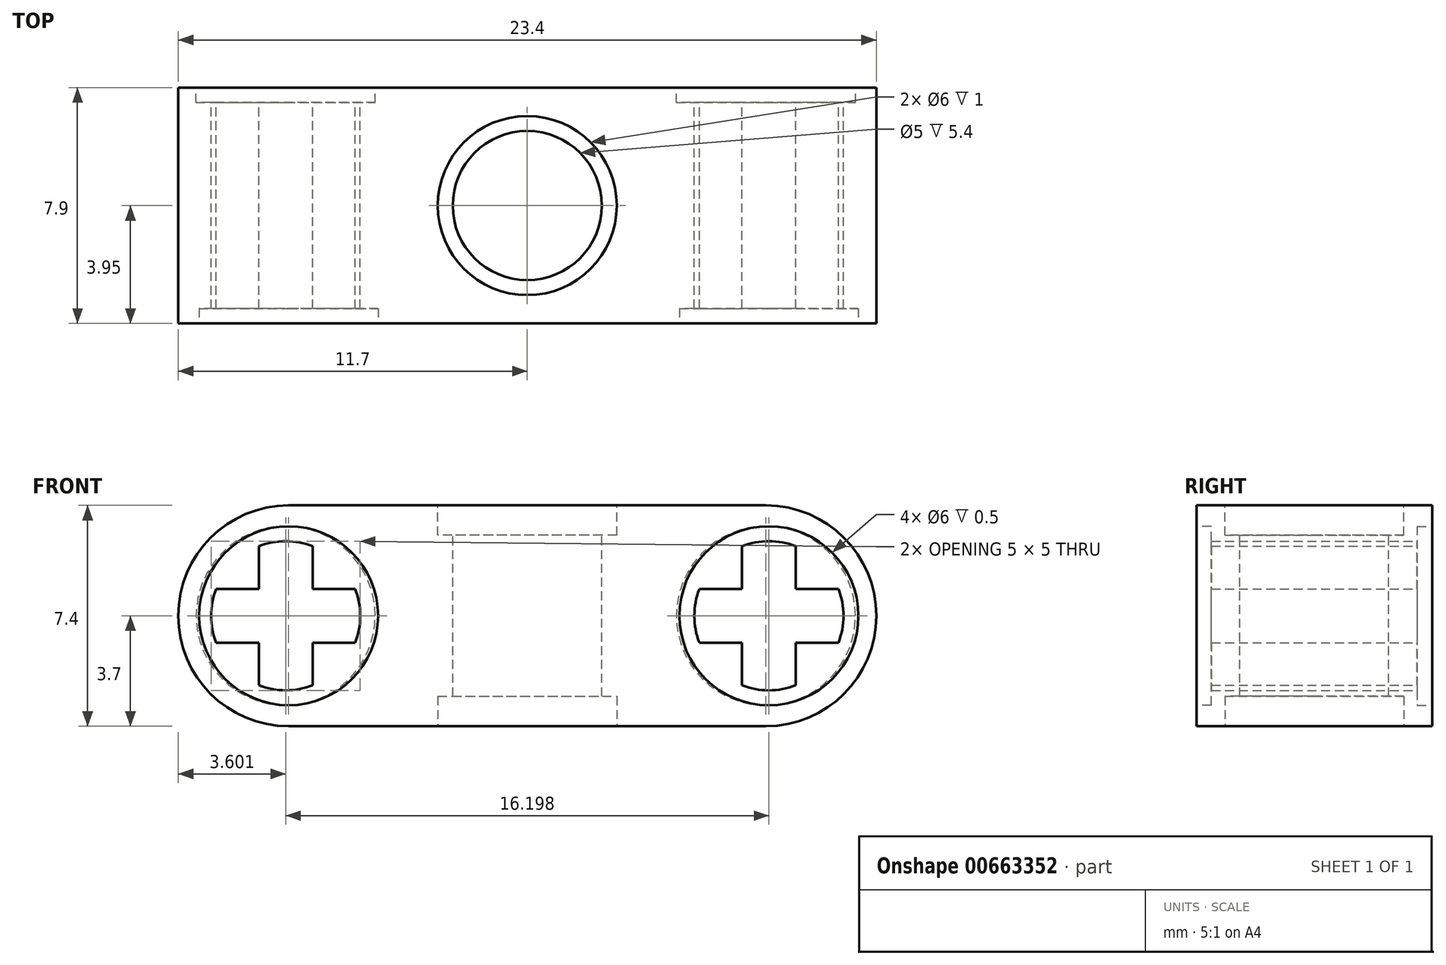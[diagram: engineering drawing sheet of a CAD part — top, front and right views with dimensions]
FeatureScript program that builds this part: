
annotation { "Feature Type Name" : "Feature", "Feature Type Description" : "" }
export const myFeature = defineFeature(function(context is Context, id is Id, definition is map)
    precondition{}
    {
        {
            var Q0;
            Q0=qCreatedBy(makeId("Front.planeOp"),FACE);
            var sketch = newSketch(context, id + "F0", { "sketchPlane" : qUnion([Q0])});
            skLineSegment(sketch, "E0.bottom", {"start": v(11.7, 3.7) * mm, "end": v(-11.7, 3.7) * mm});
            skLineSegment(sketch, "E0.top", {"start": v(11.7, -3.7) * mm, "end": v(-11.7, -3.7) * mm});
            skLineSegment(sketch, "E0.left", {"start": v(11.7, 3.7) * mm, "end": v(11.7, -3.7) * mm});
            skLineSegment(sketch, "E0.right", {"start": v(-11.7, 3.7) * mm, "end": v(-11.7, -3.7) * mm});
            skPoint(sketch, "E0.middle", {"position": v(0, 0) * mm});
            skArc(sketch, "E1", {"start": v(-9, -2.33) * mm, "mid": v(-8.1, -2.5) * mm, "end": v(-7.2, -2.33) * mm});
            skLineSegment(sketch, "E2.left", {"start": v(-7.2, 2.33) * mm, "end": v(-7.2, 0.9) * mm});
            skLineSegment(sketch, "E2.right", {"start": v(-9, 2.33) * mm, "end": v(-9, 0.9) * mm});
            skLineSegment(sketch, "E3.bottom", {"start": v(-5.77, 0.9) * mm, "end": v(-7.2, 0.9) * mm});
            skLineSegment(sketch, "E3.top", {"start": v(-5.77, -0.9) * mm, "end": v(-7.2, -0.9) * mm});
            skPoint(sketch, "E2.top.start.orphan", {"position": v(-7.2, -2.9) * mm});
            skPoint(sketch, "E4.orphan", {"position": v(-9, -2.9) * mm});
            skArc(sketch, "E5.trimOffspring", {"start": v(-10.43, 0.9) * mm, "mid": v(-10.6, 0) * mm, "end": v(-10.43, -0.9) * mm});
            skPoint(sketch, "E2.bottom.end.orphan", {"position": v(-9, 2.9) * mm});
            skPoint(sketch, "E6.orphan", {"position": v(-7.2, 2.9) * mm});
            skArc(sketch, "E7.trimOffspring", {"start": v(-7.2, 2.33) * mm, "mid": v(-8.1, 2.5) * mm, "end": v(-9, 2.33) * mm});
            skArc(sketch, "E8.trimOffspring", {"start": v(-5.77, -0.9) * mm, "mid": v(-5.6, 0) * mm, "end": v(-5.77, 0.9) * mm});
            skPoint(sketch, "E9.orphan", {"position": v(-5.6, -0.9) * mm});
            skPoint(sketch, "E10.orphan", {"position": v(-5.6, 0.9) * mm});
            skLineSegment(sketch, "E11.trimOffspring", {"start": v(-9, 0.9) * mm, "end": v(-10.43, 0.9) * mm});
            skLineSegment(sketch, "E12.trimOffspring", {"start": v(-9, -0.9) * mm, "end": v(-9, -2.33) * mm});
            skLineSegment(sketch, "E13.trimOffspring", {"start": v(-9, -0.9) * mm, "end": v(-10.43, -0.9) * mm});
            skLineSegment(sketch, "E14.trimOffspring", {"start": v(-7.2, -0.9) * mm, "end": v(-7.2, -2.33) * mm});
            skPoint(sketch, "E15.orphan", {"position": v(-10.6, 0.9) * mm});
            skPoint(sketch, "E16.orphan", {"position": v(-10.6, -0.9) * mm});
            skLineSegment(sketch, "E17", {"start": v(0, 5.75) * mm, "end": v(0, -6.04) * mm, "construction": true});
            skPoint(sketch, "E17.startSnap0", {"position": v(0, 3.7) * mm});
            skLineSegment(sketch, "E18.MirrorCS", {"start": v(7.2, 2.33) * mm, "end": v(7.2, 0.9) * mm});
            skArc(sketch, "E19.MirrorCS", {"start": v(7.2, 2.33) * mm, "mid": v(8.1, 2.5) * mm, "end": v(9, 2.33) * mm});
            skLineSegment(sketch, "E20.MirrorCS", {"start": v(9, 2.33) * mm, "end": v(9, 0.9) * mm});
            skLineSegment(sketch, "E21.MirrorCS", {"start": v(9, 0.9) * mm, "end": v(10.43, 0.9) * mm});
            skArc(sketch, "E22.MirrorCS", {"start": v(10.43, 0.9) * mm, "mid": v(10.6, 0) * mm, "end": v(10.43, -0.9) * mm});
            skLineSegment(sketch, "E23.MirrorCS", {"start": v(9, -0.9) * mm, "end": v(10.43, -0.9) * mm});
            skLineSegment(sketch, "E24.MirrorCS", {"start": v(9, -0.9) * mm, "end": v(9, -2.33) * mm});
            skArc(sketch, "E25.MirrorCS", {"start": v(9, -2.33) * mm, "mid": v(8.1, -2.5) * mm, "end": v(7.2, -2.33) * mm});
            skLineSegment(sketch, "E26.MirrorCS", {"start": v(7.2, -0.9) * mm, "end": v(7.2, -2.33) * mm});
            skLineSegment(sketch, "E27.MirrorCS", {"start": v(5.77, -0.9) * mm, "end": v(7.2, -0.9) * mm});
            skArc(sketch, "E28.MirrorCS", {"start": v(5.77, -0.9) * mm, "mid": v(5.6, 0) * mm, "end": v(5.77, 0.9) * mm});
            skLineSegment(sketch, "E29.MirrorCS", {"start": v(5.77, 0.9) * mm, "end": v(7.2, 0.9) * mm});
            skSolve(sketch);
        }
        {
            var Q0;
            Q0=qSketchRegion(id+"F0",true);
            extrude(context, id + "F1", {"entities" : qUnion([Q0]), "endBound" : BoundingType.SYMMETRIC, "depth" : 7.9 * mm, "offsetDistance" : 25 * mm});
        }
        {
            var Q0;
            Q0=makeQuery(id+"F1.opExtrude","SWEPT_EDGE",EDGE,{"disambiguationData":[OSD([sQuery(id+"F0.wireOp",EDGE,"E0.top"),sQuery(id+"F0.wireOp",EDGE,"E0.right")])]});
            var Q1;
            Q1=makeQuery(id+"F1.opExtrude","SWEPT_EDGE",EDGE,{"disambiguationData":[OSD([sQuery(id+"F0.wireOp",EDGE,"E0.bottom"),sQuery(id+"F0.wireOp",EDGE,"E0.right")])]});
            var Q2;
            Q2=makeQuery(id+"F1.opExtrude","SWEPT_EDGE",EDGE,{"disambiguationData":[OSD([sQuery(id+"F0.wireOp",EDGE,"E0.bottom"),sQuery(id+"F0.wireOp",EDGE,"E0.left")])]});
            var Q3;
            Q3=makeQuery(id+"F1.opExtrude","SWEPT_EDGE",EDGE,{"disambiguationData":[OSD([sQuery(id+"F0.wireOp",EDGE,"E0.top"),sQuery(id+"F0.wireOp",EDGE,"E0.left")])]});
            fillet(context, id + "F2", {"entities" : qUnion([Q0, Q1, Q2, Q3]), "radius" : 3.7 * mm, "tangentPropagation" : true, "allowEdgeOverflow" : false});
        }
        {
            var Q0;
            Q0=makeQuery(id+"F1.opExtrude","SWEPT_FACE",FACE,{"disambiguationData":[OSD([sQuery(id+"F0.wireOp",EDGE,"E0.bottom")])]});
            var sketch = newSketch(context, id + "F3", { "sketchPlane" : qUnion([Q0])});
            skCircle(sketch, "E30", {"center": v(0, 0) * mm, "radius": 2.5 * mm});
            skCircle(sketch, "E31", {"center": v(0, 0) * mm, "radius": 3 * mm});
            skSolve(sketch);
        }
        {
            var Q0;
            Q0=makeQuery(id+"F3.imprint","IMPRINT",FACE,{"disambiguationData":[TD([[makeQuery(id+"F3.imprint","IMPRINT",EDGE,{"derivedFrom":sQuery(id+"F3.wireOp",EDGE,"E30")}),1.0]])]});
            extrude(context, id + "F4", {"entities" : qUnion([Q0]), "operationType" : NewBodyOperationType.REMOVE, "oppositeDirection" : true, "depth" : 25 * mm, "offsetDistance" : 25 * mm});
        }
        {
            var Q0;
            Q0=makeQuery(id+"F3.imprint","IMPRINT",FACE,{"disambiguationData":[TD([[makeQuery(id+"F3.imprint","IMPRINT",EDGE,{"derivedFrom":sQuery(id+"F3.wireOp",EDGE,"E30")}),-1.0]])]});
            extrude(context, id + "F5", {"entities" : qUnion([Q0]), "operationType" : NewBodyOperationType.REMOVE, "oppositeDirection" : true, "depth" : 1 * mm, "offsetDistance" : 25 * mm});
        }
        {
            var Q0;
            Q0=makeQuery(id+"F1.opExtrude","SWEPT_FACE",FACE,{"disambiguationData":[OSD([sQuery(id+"F0.wireOp",EDGE,"E0.top")])]});
            var sketch = newSketch(context, id + "F6", { "sketchPlane" : qUnion([Q0])});
            skCircle(sketch, "E32", {"center": v(0, 0) * mm, "radius": 3 * mm});
            skSolve(sketch);
        }
        {
            var Q0;
            Q0=makeQuery(id+"F6.imprint","IMPRINT",FACE,{"disambiguationData":[TD([[makeQuery(id+"F6.imprint","IMPRINT",EDGE,{"derivedFrom":sQuery(id+"F6.wireOp",EDGE,"E32")}),1.0]])]});
            extrude(context, id + "F7", {"entities" : qUnion([Q0]), "operationType" : NewBodyOperationType.REMOVE, "oppositeDirection" : true, "depth" : 1 * mm, "offsetDistance" : 25 * mm});
        }
        {
            var Q0;
            Q0=makeQuery(id+"F1.opExtrude","CAP_FACE",FACE,{"disambiguationData":[OSD([sQuery(id+"F0.wireOp",EDGE,"E0.bottom"),sQuery(id+"F0.wireOp",EDGE,"E0.top"),sQuery(id+"F0.wireOp",EDGE,"E0.left"),sQuery(id+"F0.wireOp",EDGE,"E0.right"),sQuery(id+"F0.wireOp",EDGE,"E1"),sQuery(id+"F0.wireOp",EDGE,"E2.left"),sQuery(id+"F0.wireOp",EDGE,"E2.right"),sQuery(id+"F0.wireOp",EDGE,"E3.bottom"),sQuery(id+"F0.wireOp",EDGE,"E3.top"),sQuery(id+"F0.wireOp",EDGE,"E5.trimOffspring"),sQuery(id+"F0.wireOp",EDGE,"E7.trimOffspring"),sQuery(id+"F0.wireOp",EDGE,"E8.trimOffspring"),sQuery(id+"F0.wireOp",EDGE,"E11.trimOffspring"),sQuery(id+"F0.wireOp",EDGE,"E12.trimOffspring"),sQuery(id+"F0.wireOp",EDGE,"E13.trimOffspring"),sQuery(id+"F0.wireOp",EDGE,"E14.trimOffspring"),sQuery(id+"F0.wireOp",EDGE,"E18.MirrorCS"),sQuery(id+"F0.wireOp",EDGE,"E19.MirrorCS"),sQuery(id+"F0.wireOp",EDGE,"E20.MirrorCS"),sQuery(id+"F0.wireOp",EDGE,"E21.MirrorCS"),sQuery(id+"F0.wireOp",EDGE,"E22.MirrorCS"),sQuery(id+"F0.wireOp",EDGE,"E23.MirrorCS"),sQuery(id+"F0.wireOp",EDGE,"E24.MirrorCS"),sQuery(id+"F0.wireOp",EDGE,"E25.MirrorCS"),sQuery(id+"F0.wireOp",EDGE,"E26.MirrorCS"),sQuery(id+"F0.wireOp",EDGE,"E27.MirrorCS"),sQuery(id+"F0.wireOp",EDGE,"E28.MirrorCS"),sQuery(id+"F0.wireOp",EDGE,"E29.MirrorCS")])],"isStart":false});
            var sketch = newSketch(context, id + "F8", { "sketchPlane" : qUnion([Q0])});
            skCircle(sketch, "E33", {"center": v(-8, 0) * mm, "radius": 3 * mm});
            skCircle(sketch, "E34", {"center": v(8.1, 0) * mm, "radius": 3 * mm});
            skSolve(sketch);
        }
        {
            var Q0;
            Q0=qSketchRegion(id+"F8",true);
            extrude(context, id + "F9", {"entities" : qUnion([Q0]), "operationType" : NewBodyOperationType.REMOVE, "oppositeDirection" : true, "depth" : 0.5 * mm, "offsetDistance" : 25 * mm});
        }
        {
            var Q0;
            Q0=makeQuery(id+"F1.opExtrude","CAP_FACE",FACE,{"disambiguationData":[OSD([sQuery(id+"F0.wireOp",EDGE,"E0.bottom"),sQuery(id+"F0.wireOp",EDGE,"E0.top"),sQuery(id+"F0.wireOp",EDGE,"E0.left"),sQuery(id+"F0.wireOp",EDGE,"E0.right"),sQuery(id+"F0.wireOp",EDGE,"E1"),sQuery(id+"F0.wireOp",EDGE,"E2.left"),sQuery(id+"F0.wireOp",EDGE,"E2.right"),sQuery(id+"F0.wireOp",EDGE,"E3.bottom"),sQuery(id+"F0.wireOp",EDGE,"E3.top"),sQuery(id+"F0.wireOp",EDGE,"E5.trimOffspring"),sQuery(id+"F0.wireOp",EDGE,"E7.trimOffspring"),sQuery(id+"F0.wireOp",EDGE,"E8.trimOffspring"),sQuery(id+"F0.wireOp",EDGE,"E11.trimOffspring"),sQuery(id+"F0.wireOp",EDGE,"E12.trimOffspring"),sQuery(id+"F0.wireOp",EDGE,"E13.trimOffspring"),sQuery(id+"F0.wireOp",EDGE,"E14.trimOffspring"),sQuery(id+"F0.wireOp",EDGE,"E18.MirrorCS"),sQuery(id+"F0.wireOp",EDGE,"E19.MirrorCS"),sQuery(id+"F0.wireOp",EDGE,"E20.MirrorCS"),sQuery(id+"F0.wireOp",EDGE,"E21.MirrorCS"),sQuery(id+"F0.wireOp",EDGE,"E22.MirrorCS"),sQuery(id+"F0.wireOp",EDGE,"E23.MirrorCS"),sQuery(id+"F0.wireOp",EDGE,"E24.MirrorCS"),sQuery(id+"F0.wireOp",EDGE,"E25.MirrorCS"),sQuery(id+"F0.wireOp",EDGE,"E26.MirrorCS"),sQuery(id+"F0.wireOp",EDGE,"E27.MirrorCS"),sQuery(id+"F0.wireOp",EDGE,"E28.MirrorCS"),sQuery(id+"F0.wireOp",EDGE,"E29.MirrorCS")])],"isStart":true});
            var sketch = newSketch(context, id + "F10", { "sketchPlane" : qUnion([Q0])});
            skCircle(sketch, "E35", {"center": v(-8, 0) * mm, "radius": 3 * mm});
            skCircle(sketch, "E36", {"center": v(8.1, 0) * mm, "radius": 3 * mm});
            skSolve(sketch);
        }
        {
            var Q0;
            Q0=qSketchRegion(id+"F10",true);
            extrude(context, id + "F11", {"entities" : qUnion([Q0]), "operationType" : NewBodyOperationType.REMOVE, "oppositeDirection" : true, "depth" : .5 * mm, "offsetDistance" : 25 * mm});
        }
    });
